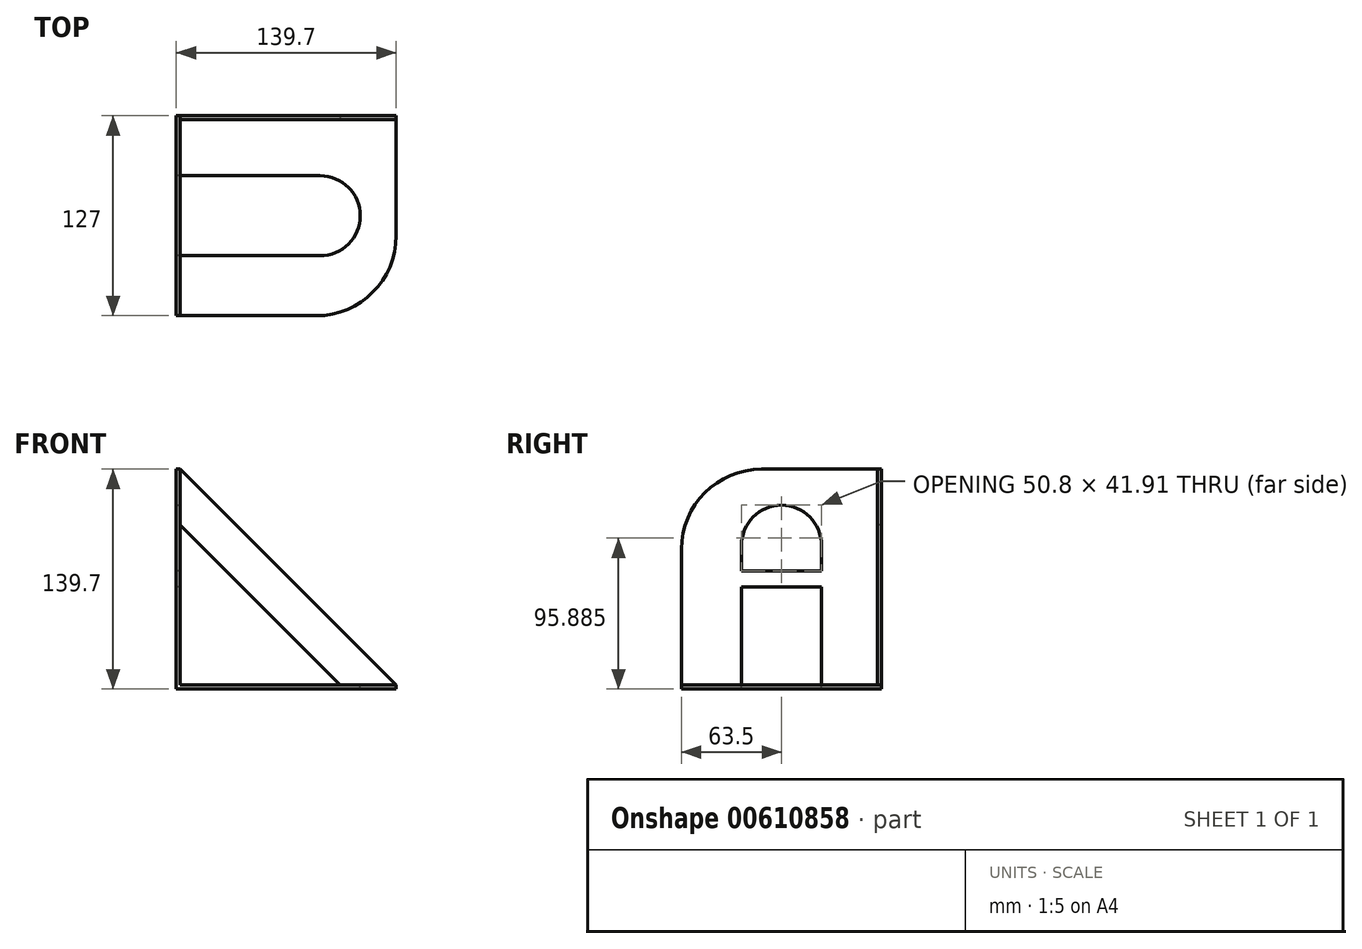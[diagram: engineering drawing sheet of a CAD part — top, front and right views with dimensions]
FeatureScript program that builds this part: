
annotation { "Feature Type Name" : "Feature", "Feature Type Description" : "" }
export const myFeature = defineFeature(function(context is Context, id is Id, definition is map)
    precondition{}
    {
        {
            var Q0;
            Q0=qCreatedBy(makeId("Top.planeOp"),FACE);
            var sketch = newSketch(context, id + "F0", { "sketchPlane" : qUnion([Q0])});
            skLineSegment(sketch, "E0.bottom", {"start": v(0, 0) * mm, "end": v(-139.7, 0) * mm});
            skLineSegment(sketch, "E0.top", {"start": v(0, -127) * mm, "end": v(-139.7, -127) * mm});
            skLineSegment(sketch, "E0.left", {"start": v(0, 0) * mm, "end": v(0, -127) * mm});
            skLineSegment(sketch, "E0.right", {"start": v(-139.7, 0) * mm, "end": v(-139.7, -127) * mm});
            skSolve(sketch);
        }
        {
            var Q0;
            Q0=qSketchRegion(id+"F0",true);
            extrude(context, id + "F1", {"entities" : qUnion([Q0]), "depth" : 139.7 * mm});
        }
        {
            var Q0;
            Q0=makeQuery(id+"F1.opExtrude","SWEPT_FACE",FACE,{"disambiguationData":[OSD([sQuery(id+"F0.wireOp",EDGE,"E0.top")])]});
            var sketch = newSketch(context, id + "F2", { "sketchPlane" : qUnion([Q0])});
            skLineSegment(sketch, "E1.bottom", {"start": v(0, 139.7) * mm, "end": v(-137.16, 139.7) * mm});
            skLineSegment(sketch, "E1.top", {"start": v(0, 2.54) * mm, "end": v(-137.16, 2.54) * mm});
            skLineSegment(sketch, "E1.left", {"start": v(0, 139.7) * mm, "end": v(0, 2.54) * mm});
            skLineSegment(sketch, "E1.right", {"start": v(-137.16, 139.7) * mm, "end": v(-137.16, 2.54) * mm});
            skSolve(sketch);
        }
        {
            var Q0;
            Q0=qSketchRegion(id+"F2",true);
            extrude(context, id + "F3", {"entities" : qUnion([Q0]), "operationType" : NewBodyOperationType.REMOVE, "oppositeDirection" : true, "depth" : 124.46 * mm});
        }
        {
            var Q0;
            Q0=makeQuery(id+"F3.boolean.opBoolean","COPY",FACE,{"derivedFrom":makeQuery(id+"F3.opExtrude","CAP_FACE",FACE,{"disambiguationData":[OSD([sQuery(id+"F2.wireOp",EDGE,"E1.bottom"),sQuery(id+"F2.wireOp",EDGE,"E1.top"),sQuery(id+"F2.wireOp",EDGE,"E1.left"),sQuery(id+"F2.wireOp",EDGE,"E1.right")])],"isStart":false})});
            var sketch = newSketch(context, id + "F4", { "sketchPlane" : qUnion([Q0])});
            skLineSegment(sketch, "E2", {"start": v(-137.16, 139.7) * mm, "end": v(0, 2.54) * mm});
            skLineSegment(sketch, "E3", {"start": v(0, 2.54) * mm, "end": v(55.8, 142.75) * mm});
            skLineSegment(sketch, "E4", {"start": v(55.8, 142.75) * mm, "end": v(-6.92, 178.29) * mm});
            skLineSegment(sketch, "E5", {"start": v(-6.92, 178.29) * mm, "end": v(-137.16, 139.7) * mm});
            skSolve(sketch);
        }
        {
            var Q0;
            Q0=qSketchRegion(id+"F4",true);
            extrude(context, id + "F5", {"entities" : qUnion([Q0]), "operationType" : NewBodyOperationType.REMOVE, "oppositeDirection" : true, "depth" : 25.4 * mm});
        }
        {
            var Q0;
            Q0=makeQuery(id+"F3.boolean.opBoolean","COPY",FACE,{"derivedFrom":makeQuery(id+"F3.opExtrude","CAP_FACE",FACE,{"disambiguationData":[OSD([sQuery(id+"F2.wireOp",EDGE,"E1.bottom"),sQuery(id+"F2.wireOp",EDGE,"E1.top"),sQuery(id+"F2.wireOp",EDGE,"E1.left"),sQuery(id+"F2.wireOp",EDGE,"E1.right")])],"isStart":false})});
            var sketch = newSketch(context, id + "F6", { "sketchPlane" : qUnion([Q0])});
            skLineSegment(sketch, "E6", {"start": v(-137.16, 2.54) * mm, "end": v(-35.56, 2.54) * mm});
            skLineSegment(sketch, "E7", {"start": v(-35.56, 2.54) * mm, "end": v(-137.16, 104.14) * mm});
            skLineSegment(sketch, "E8", {"start": v(-137.16, 104.14) * mm, "end": v(-137.16, 2.54) * mm});
            skSolve(sketch);
        }
        {
            var Q0;
            Q0=qSketchRegion(id+"F6",true);
            extrude(context, id + "F7", {"entities" : qUnion([Q0]), "operationType" : NewBodyOperationType.REMOVE, "oppositeDirection" : true, "depth" : 25.4 * mm});
        }
        {
            var Q0;
            Q0=makeQuery(id+"F7.boolean.opBoolean","MERGE",FACE,{"derivedFrom":[makeQuery(id+"F3.boolean.opBoolean","COPY",FACE,{"derivedFrom":makeQuery(id+"F3.opExtrude","SWEPT_FACE",FACE,{"disambiguationData":[OSD([sQuery(id+"F2.wireOp",EDGE,"E1.top")])]})}),makeQuery(id+"F7.opExtrude","SWEPT_FACE",FACE,{"disambiguationData":[OSD([sQuery(id+"F6.wireOp",EDGE,"E6")])]})]});
            var sketch = newSketch(context, id + "F8", { "sketchPlane" : qUnion([Q0])});
            skLineSegment(sketch, "E9", {"start": v(-137.16, -88.9) * mm, "end": v(-48.26, -88.9) * mm});
            skLineSegment(sketch, "E10", {"start": v(-48.26, -38.1) * mm, "end": v(-137.16, -38.1) * mm});
            skLineSegment(sketch, "E11", {"start": v(-137.16, -38.1) * mm, "end": v(-137.16, -88.9) * mm});
            skArc(sketch, "E12", {"start": v(-48.26, -88.9) * mm, "mid": v(-22.86, -63.5) * mm, "end": v(-48.26, -38.1) * mm});
            skSolve(sketch);
        }
        {
            var Q0;
            Q0=qSketchRegion(id+"F8",true);
            extrude(context, id + "F9", {"entities" : qUnion([Q0]), "operationType" : NewBodyOperationType.REMOVE, "oppositeDirection" : true, "depth" : 25.4 * mm});
        }
        {
            var Q0;
            Q0=makeQuery(id+"F9.boolean.opBoolean","MERGE",FACE,{"derivedFrom":[makeQuery(id+"F7.boolean.opBoolean","MERGE",FACE,{"derivedFrom":[makeQuery(id+"F3.boolean.opBoolean","COPY",FACE,{"derivedFrom":makeQuery(id+"F3.opExtrude","SWEPT_FACE",FACE,{"disambiguationData":[OSD([sQuery(id+"F2.wireOp",EDGE,"E1.right")])]})}),makeQuery(id+"F7.opExtrude","SWEPT_FACE",FACE,{"disambiguationData":[OSD([sQuery(id+"F6.wireOp",EDGE,"E8")])]})]}),makeQuery(id+"F9.opExtrude","SWEPT_FACE",FACE,{"disambiguationData":[OSD([sQuery(id+"F8.wireOp",EDGE,"E11")])]})]});
            var sketch = newSketch(context, id + "F10", { "sketchPlane" : qUnion([Q0])});
            skLineSegment(sketch, "E13", {"start": v(-38.1, 2.54) * mm, "end": v(-38.1, 91.44) * mm});
            skLineSegment(sketch, "E14", {"start": v(-88.9, 2.54) * mm, "end": v(-88.9, 91.44) * mm});
            skArc(sketch, "E15", {"start": v(-38.1, 91.44) * mm, "mid": v(-63.5, 116.84) * mm, "end": v(-88.9, 91.44) * mm});
            skSolve(sketch);
        }
        {
            var Q0;
            Q0=qSketchRegion(id+"F10",true);
            var Q1;
            Q1=makeQuery(id+"F10.imprint","IMPRINT",FACE,{"disambiguationData":[TD([[makeQuery(id+"F10.imprint","IMPRINT",EDGE,{"derivedFrom":sQuery(id+"F10.wireOp",EDGE,"E13")}),1.0]])]});
            extrude(context, id + "F11", {"entities" : qUnion([Q0, Q1]), "operationType" : NewBodyOperationType.REMOVE, "oppositeDirection" : true, "depth" : 25.4 * mm});
        }
        {
            var Q0;
            Q0=makeQuery(id+"F1.opExtrude","SWEPT_EDGE",EDGE,{"disambiguationData":[OSD([sQuery(id+"F0.wireOp",EDGE,"E0.top"),sQuery(id+"F0.wireOp",EDGE,"E0.left")])]});
            var Q1;
            Q1=makeQuery(id+"F1.opExtrude","CAP_EDGE",EDGE,{"disambiguationData":[OSD([sQuery(id+"F0.wireOp",EDGE,"E0.top")])],"isStart":false});
            fillet(context, id + "F12", {"entities" : qUnion([Q0, Q1]), "radius" : 50.8 * mm, "tangentPropagation" : true, "allowEdgeOverflow" : false});
        }
        {
            var Q0;
            Q0=makeQuery(id+"F1.opExtrude","SWEPT_FACE",FACE,{"disambiguationData":[OSD([sQuery(id+"F0.wireOp",EDGE,"E0.right")])]});
            var sketch = newSketch(context, id + "F13", { "sketchPlane" : qUnion([Q0])});
            skPoint(sketch, "E16", {"position": v(0, 69.85) * mm});
            skPoint(sketch, "E17", {"position": v(0, 139.7) * mm});
            skPoint(sketch, "E18", {"position": v(127, 69.85) * mm});
            skLineSegment(sketch, "E19", {"start": v(0, 69.85) * mm, "end": v(38.1, 69.85) * mm});
            skLineSegment(sketch, "E20", {"start": v(127, 69.85) * mm, "end": v(88.9, 69.85) * mm});
            skLineSegment(sketch, "E21", {"start": v(0, 74.93) * mm, "end": v(38.1, 74.93) * mm});
            skLineSegment(sketch, "E22", {"start": v(0, 64.77) * mm, "end": v(38.1, 64.77) * mm});
            skLineSegment(sketch, "E23", {"start": v(88.9, 64.77) * mm, "end": v(127, 64.77) * mm});
            skLineSegment(sketch, "E24", {"start": v(88.9, 74.93) * mm, "end": v(127, 74.93) * mm});
            skLineSegment(sketch, "E25", {"start": v(38.1, 74.93) * mm, "end": v(88.9, 74.93) * mm});
            skLineSegment(sketch, "E26", {"start": v(38.1, 64.77) * mm, "end": v(88.9, 64.77) * mm});
            skSolve(sketch);
        }
        {
            var Q0;
            {var subQ8=sQuery(id+"F13.wireOp",EDGE,"E25");Q0=makeQuery(id+"F13.imprint","IMPRINT",FACE,{"disambiguationData":[TD([[makeQuery(id+"F13.imprint","IMPRINT",EDGE,{"derivedFrom":subQ8}),-1.0]])]});}
            extrude(context, id + "F14", {"entities" : qUnion([Q0]), "operationType" : NewBodyOperationType.ADD, "oppositeDirection" : true, "depth" : 2.54 * mm, "offsetDistance" : 25.4 * mm});
        }
    });
